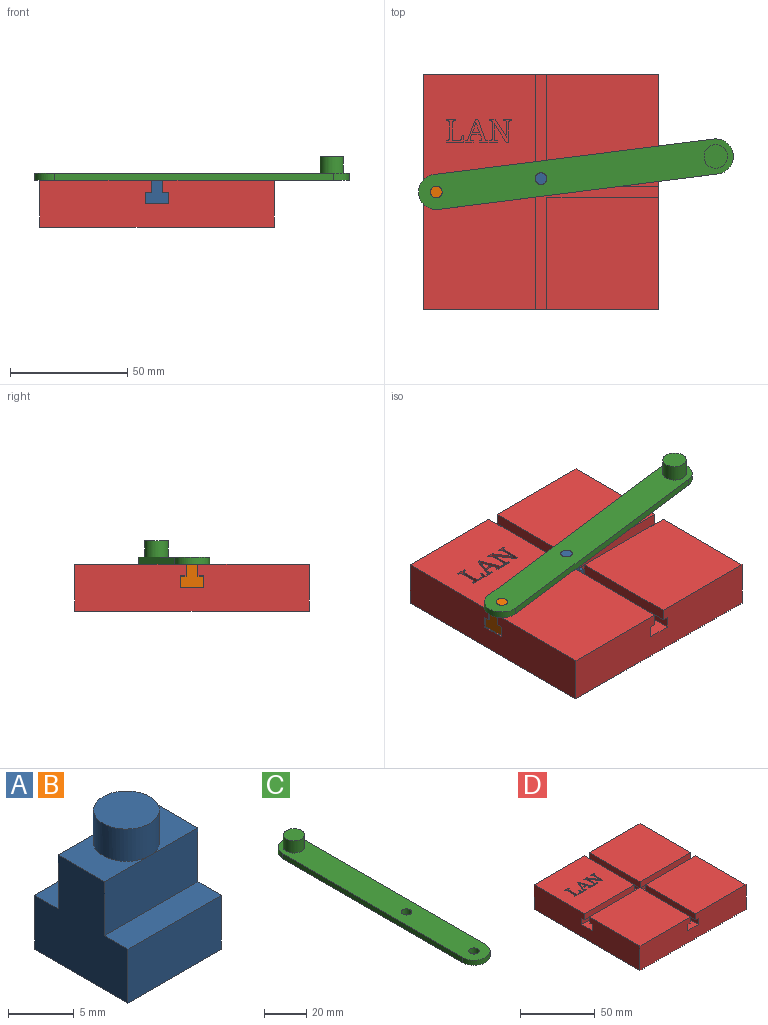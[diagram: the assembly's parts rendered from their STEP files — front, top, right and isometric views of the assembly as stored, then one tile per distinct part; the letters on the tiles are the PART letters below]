
ASSEMBLY  parts=4 mates=4
PART A: 13 faces, bbox 10x10x13 mm
  f0: plane 5x4.83mm, normal (0,0,1), area 14.3mm2, adj f2,f8,f10,f11
  f1: plane 5.17x5mm, normal (0,0,1), area 16mm2, adj f2,f8,f9,f11
  f2: plane 10x5mm, normal (0,1,0), area 50mm2, adj f0,f1,f3,f9,f10
  f3: plane 10x2.5mm, normal (0,0,1), area 25mm2, adj f2,f4,f9,f10
  f4: plane 10x5mm, normal (0,1,0), area 50mm2, adj f3,f5,f9,f10
  f5: plane 10x10mm, normal (0,0,-1), area 100mm2, adj f4,f6,f9,f10
  f6: plane 10x5mm, normal (0,-1,0), area 50mm2, adj f5,f7,f9,f10
  f7: plane 10x2.5mm, normal (0,0,1), area 25mm2, adj f6,f8,f9,f10
  f8: plane 10x5mm, normal (0,-1,0), area 50mm2, adj f0,f1,f7,f9,f10
  f9: plane 10x10mm, normal (1,0,0), area 75mm2, adj f1,f2,f3,f4,f5,f6,f7,f8
  f10: plane 10x10mm, normal (-1,0,0), area 75mm2, adj f0,f2,f3,f4,f5,f6,f7,f8
  f11: cylinder r=2.5mm len=5mm, axis (0,0,-1), area 47.1mm2, adj f0,f1,f12
  f12: plane 5x5mm, normal (0,0,1), area 19.6mm2, adj f11
PART B: same geometry as A
PART C: 10 faces, bbox 15x135x10 mm
  f0: plane 120x3mm, normal (1,0,0), area 360mm2, adj f1,f3,f6,f7
  f1: cylinder r=7.5mm len=15mm, axis (0,0,-1), area 70.7mm2, adj f0,f2,f6,f7
  f2: plane 120x3mm, normal (-1,0,0), area 360mm2, adj f1,f3,f6,f7
  f3: cylinder r=7.5mm len=15mm, axis (0,0,-1), area 70.7mm2, adj f0,f2,f6,f7
  f4: cylinder r=2.5mm len=5mm, axis (0,0,-1), area 47.1mm2, adj f6,f7
  f5: cylinder r=2.5mm len=5mm, axis (0,0,-1), area 47.1mm2, adj f6,f7
  f6: plane 135x15mm, normal (0,0,1), area 1858.9mm2, adj f0,f1,f2,f3,f4,f5,f8
  f7: plane 135x15mm, normal (0,0,-1), area 1937.4mm2, adj f0,f1,f2,f3,f4,f5
  f8: cylinder r=5mm len=10mm, axis (0,0,-1), area 219.9mm2, adj f6,f9
  f9: plane 10x10mm, normal (0,0,1), area 78.5mm2, adj f8
PART D: 144 faces, bbox 100x100x20 mm
  f0: plane 47.5x47.5mm, normal (0,0,1), area 2166.6mm2, adj f12,f13,f16,f25,f38,f39,f40,f41
  f1: plane 47.5x47.5mm, normal (0,0,1), area 2256.2mm2, adj f6,f10,f11,f27
  f2: plane 47.5x47.5mm, normal (0,0,1), area 2256.3mm2, adj f5,f10,f13,f23
  f3: plane 47.5x47.5mm, normal (0,0,-1), area 231.2mm2, adj f12,f13,f16,f21,f22,f25
  f4: plane 47.5x47.5mm, normal (0,0,-1), area 231.3mm2, adj f6,f7,f10,f11,f27,f29
  f5: plane 47.5x5mm, normal (1,0,0), area 237.5mm2, adj f2,f10,f15,f23
  f6: plane 47.5x5mm, normal (-1,0,0), area 237.5mm2, adj f1,f4,f10,f27
  f7: plane 45x5mm, normal (-1,0,0), area 225mm2, adj f4,f10,f20,f29
  f8: plane 45x5mm, normal (1,0,0), area 225mm2, adj f10,f15,f20,f24
  f9: plane 47.5x47.5mm, normal (0,0,1), area 2256.3mm2, adj f11,f12,f17,f26
  f10: plane 100x20mm, normal (0,-1,0), area 1925mm2, adj f1,f2,f4,f5,f6,f7,f8,f11
  f11: plane 100x20mm, normal (1,0,0), area 1925mm2, adj f1,f4,f9,f10,f12,f14,f18,f20
  f12: plane 100x20mm, normal (0,1,0), area 1925mm2, adj f0,f3,f9,f11,f13,f14,f16,f17
  f13: plane 100x20mm, normal (-1,0,0), area 1925mm2, adj f0,f2,f3,f10,f12,f14,f15,f20
  f14: plane 100x100mm, normal (0,0,-1), area 10000mm2, adj f10,f11,f12,f13
  f15: plane 47.5x47.5mm, normal (0,0,-1), area 231.2mm2, adj f5,f8,f10,f13,f23,f24
  f16: plane 47.5x5mm, normal (1,0,0), area 237.5mm2, adj f0,f3,f12,f25
  f17: plane 47.5x5mm, normal (-1,0,0), area 237.5mm2, adj f9,f12,f18,f26
  f18: plane 47.5x47.5mm, normal (0,0,-1), area 231.2mm2, adj f11,f12,f17,f19,f26,f28
  f19: plane 45x5mm, normal (-1,0,0), area 225mm2, adj f12,f18,f20,f28
  f20: plane 100x100mm, normal (0,0,1), area 1900mm2, adj f7,f8,f10,f11,f12,f13,f19,f21
  f21: plane 45x5mm, normal (1,0,0), area 225mm2, adj f3,f12,f20,f22
  f22: plane 45x5mm, normal (0,-1,0), area 225mm2, adj f3,f13,f20,f21
  f23: plane 47.5x5mm, normal (0,1,0), area 237.5mm2, adj f2,f5,f13,f15
  f24: plane 45x5mm, normal (0,1,0), area 225mm2, adj f8,f13,f15,f20
  f25: plane 47.5x5mm, normal (0,-1,0), area 237.5mm2, adj f0,f3,f13,f16
  f26: plane 47.5x5mm, normal (0,-1,0), area 237.5mm2, adj f9,f11,f17,f18
  f27: plane 47.5x5mm, normal (0,1,0), area 237.5mm2, adj f1,f4,f6,f11
  f28: plane 45x5mm, normal (0,-1,0), area 225mm2, adj f11,f18,f19,f20
  f29: plane 45x5mm, normal (0,1,0), area 225mm2, adj f4,f7,f11,f20
  f30: extruded ~3x1.15mm, area 3.6mm2, adj f31,f69,f70,f143
  f31: plane 3x2.41mm, normal (0.94,0.33,0), area 7.7mm2, adj f30,f32,f70,f143
  f32: plane 3.1x3mm, normal (0,-1,0), area 9.3mm2, adj f31,f33,f70,f143
  f33: plane 3x2.53mm, normal (-0.94,0.35,0), area 8.1mm2, adj f32,f34,f70,f143
  f34: extruded ~3x0.59mm, area 1.9mm2, adj f33,f35,f70,f143
  f35: extruded ~3x0.51mm, area 1.6mm2, adj f34,f36,f70,f143
  f36: extruded ~3x0.47mm, area 1.5mm2, adj f35,f37,f70,f143
  f37: extruded ~3x0.48mm, area 1.5mm2, adj f36,f69,f70,f143
  f38: plane 3x1.45mm, normal (-0.94,0.34,0), area 4.6mm2, adj f0,f39,f68,f70
  f39: plane 3.62x3mm, normal (0,1,0), area 10.9mm2, adj f0,f38,f40,f70
  f40: plane 3x1.54mm, normal (0.94,0.34,0), area 4.9mm2, adj f0,f39,f41,f70
  f41: extruded ~3x0.28mm, area 0.9mm2, adj f0,f40,f42,f70
  f42: extruded ~3x0.24mm, area 0.7mm2, adj f0,f41,f43,f70
  f43: extruded ~3x0.83mm, area 3.6mm2, adj f0,f42,f44,f70
  f44: plane 3x0.32mm, normal (0,-1,0), area 0.9mm2, adj f0,f43,f45,f70
  f45: plane 3x0.58mm, normal (1,0,0), area 1.7mm2, adj f0,f44,f46,f70
  f46: plane 3.79x3mm, normal (0,1,0), area 11.4mm2, adj f0,f45,f47,f70
  f47: plane 3x0.58mm, normal (-1,0,0), area 1.7mm2, adj f0,f46,f48,f70
  f48: plane 3x0.18mm, normal (0,-1,0), area 0.5mm2, adj f0,f47,f49,f70
  f49: extruded ~3x0.35mm, area 1.1mm2, adj f0,f48,f50,f70
  f50: extruded ~3x0.26mm, area 0.9mm2, adj f0,f49,f51,f70
  f51: extruded ~3x0.23mm, area 0.9mm2, adj f0,f50,f52,f70
  f52: extruded ~3x0.36mm, area 1.2mm2, adj f0,f51,f53,f70
  f53: plane 8.52x3.11mm, normal (-0.94,-0.34,0), area 27.2mm2, adj f0,f52,f54,f70
  f54: plane 3x1.08mm, normal (0,-1,0), area 3.2mm2, adj f0,f53,f55,f70
  f55: plane 8.18x3.05mm, normal (0.94,-0.35,0), area 26.2mm2, adj f0,f54,f56,f70
  f56: extruded ~3x0.54mm, area 1.8mm2, adj f0,f55,f57,f70
  f57: extruded ~3x0.33mm, area 1.2mm2, adj f0,f56,f58,f70
  f58: extruded ~3x0.26mm, area 0.9mm2, adj f0,f57,f59,f70
  f59: extruded ~3x0.34mm, area 1mm2, adj f0,f58,f60,f70
  f60: plane 3x0.26mm, normal (0,-1,0), area 0.8mm2, adj f0,f59,f61,f70
  f61: plane 3x0.58mm, normal (1,0,0), area 1.7mm2, adj f0,f60,f62,f70
  f62: plane 3.36x3mm, normal (0,1,0), area 10.1mm2, adj f0,f61,f63,f70
  f63: plane 3x0.58mm, normal (-1,0,0), area 1.7mm2, adj f0,f62,f64,f70
  f64: plane 3x0.32mm, normal (0,-1,0), area 0.9mm2, adj f0,f63,f65,f70
  f65: extruded ~3x0.69mm, area 2.2mm2, adj f0,f64,f66,f70
  f66: extruded ~3x0.51mm, area 1.7mm2, adj f0,f65,f67,f70
  f67: extruded ~3x0.27mm, area 0.8mm2, adj f0,f66,f68,f70
  f68: extruded ~3x0.32mm, area 1mm2, adj f0,f38,f67,f70
  f69: extruded ~3x1.03mm, area 3.2mm2, adj f30,f37,f70,f143
  f70: plane 9.83x9.71mm, normal (0,0,1), area 27.1mm2, adj f30,f31,f32,f33,f34,f35,f36,f37
  f71: plane 7.94x5.16mm, normal (0.84,0.55,0), area 28.4mm2, adj f0,f72,f110,f111
  f72: plane 3x0.98mm, normal (0,1,0), area 2.9mm2, adj f0,f71,f73,f111
  f73: plane 8.26x3mm, normal (-1,0,0), area 24.8mm2, adj f0,f72,f74,f111
  f74: extruded ~3x0.52mm, area 1.6mm2, adj f0,f73,f75,f111
  f75: extruded ~3x0.3mm, area 1.2mm2, adj f0,f74,f76,f111
  f76: extruded ~3x0.36mm, area 1.2mm2, adj f0,f75,f77,f111
  f77: extruded ~3x0.44mm, area 1.3mm2, adj f0,f76,f78,f111
  f78: plane 3x0.17mm, normal (0,1,0), area 0.5mm2, adj f0,f77,f79,f111
  f79: plane 3x0.58mm, normal (-1,0,0), area 1.7mm2, adj f0,f78,f80,f111
  f80: plane 3.46x3mm, normal (0,-1,0), area 10.4mm2, adj f0,f79,f81,f111
  f81: plane 3x0.58mm, normal (1,0,0), area 1.7mm2, adj f0,f80,f82,f111
  f82: plane 3x0.18mm, normal (0,1,0), area 0.5mm2, adj f0,f81,f83,f111
  f83: extruded ~3x0.43mm, area 1.3mm2, adj f0,f82,f84,f111
  f84: extruded ~3x0.36mm, area 1.2mm2, adj f0,f83,f85,f111
  f85: extruded ~3x0.29mm, area 1.1mm2, adj f0,f84,f86,f111
  f86: extruded ~3x0.49mm, area 1.5mm2, adj f0,f85,f87,f111
  f87: plane 6.1x3mm, normal (1,0,0), area 18.3mm2, adj f0,f86,f88,f111
  f88: plane 7.61x4.93mm, normal (-0.84,-0.54,0), area 27.2mm2, adj f0,f87,f89,f111
  f89: plane 3x2.52mm, normal (0,-1,0), area 7.6mm2, adj f0,f88,f90,f111
  f90: plane 3x0.58mm, normal (1,0,0), area 1.7mm2, adj f0,f89,f91,f111
  f91: plane 3x0.17mm, normal (0,1,0), area 0.5mm2, adj f0,f90,f92,f111
  f92: extruded ~3x0.43mm, area 1.3mm2, adj f0,f91,f93,f111
  f93: extruded ~3x0.36mm, area 1.2mm2, adj f0,f92,f94,f111
  f94: extruded ~3x0.29mm, area 1.1mm2, adj f0,f93,f95,f111
  f95: extruded ~3x0.49mm, area 1.5mm2, adj f0,f94,f96,f111
  f96: plane 6.75x3mm, normal (1,0,0), area 20.3mm2, adj f0,f95,f97,f111
  f97: extruded ~3x0.52mm, area 1.6mm2, adj f0,f96,f98,f111
  f98: extruded ~3x0.3mm, area 1.2mm2, adj f0,f97,f99,f111
  f99: extruded ~3x0.36mm, area 1.2mm2, adj f0,f98,f100,f111
  f100: extruded ~3x0.44mm, area 1.3mm2, adj f0,f99,f101,f111
  f101: plane 3x0.17mm, normal (0,-1,0), area 0.5mm2, adj f0,f100,f102,f111
  f102: plane 3x0.58mm, normal (1,0,0), area 1.7mm2, adj f0,f101,f103,f111
  f103: plane 3.46x3mm, normal (0,1,0), area 10.4mm2, adj f0,f102,f104,f111
  f104: plane 3x0.58mm, normal (-1,0,0), area 1.7mm2, adj f0,f103,f105,f111
  f105: plane 3x0.18mm, normal (0,-1,0), area 0.5mm2, adj f0,f104,f106,f111
  f106: extruded ~3x0.44mm, area 1.3mm2, adj f0,f105,f107,f111
  f107: extruded ~3x0.36mm, area 1.2mm2, adj f0,f106,f108,f111
  f108: extruded ~3x0.3mm, area 1.2mm2, adj f0,f107,f109,f111
  f109: extruded ~3x0.52mm, area 1.6mm2, adj f0,f108,f110,f111
  f110: plane 6.37x3mm, normal (-1,0,0), area 19.1mm2, adj f0,f71,f109,f111
  f111: plane 9.83x9.59mm, normal (0,0,1), area 34mm2, adj f71,f72,f73,f74,f75,f76,f77,f78
  f112: plane 3x0.58mm, normal (1,0,0), area 1.7mm2, adj f0,f113,f141,f142
  f113: plane 7.38x3mm, normal (0,1,0), area 22.1mm2, adj f0,f112,f114,f142
  f114: plane 3x2.96mm, normal (-1,0.03,0), area 8.9mm2, adj f0,f113,f115,f142
  f115: plane 3x0.72mm, normal (0,-1,0), area 2.2mm2, adj f0,f114,f116,f142
  f116: plane 3x1.03mm, normal (0.99,-0.13,0), area 3.1mm2, adj f0,f115,f117,f142
  f117: extruded ~3x0.44mm, area 1.4mm2, adj f0,f116,f118,f142
  f118: extruded ~3x0.4mm, area 1.4mm2, adj f0,f117,f119,f142
  f119: extruded ~3x0.36mm, area 1.4mm2, adj f0,f118,f120,f142
  f120: extruded ~3x0.53mm, area 1.6mm2, adj f0,f119,f121,f142
  f121: plane 3x2.72mm, normal (0,-1,0), area 8.1mm2, adj f0,f120,f122,f142
  f122: plane 7.63x3mm, normal (-1,0,0), area 22.9mm2, adj f0,f121,f123,f142
  f123: extruded ~3x0.49mm, area 1.5mm2, adj f0,f122,f124,f142
  f124: extruded ~3x0.29mm, area 1.1mm2, adj f0,f123,f125,f142
  f125: extruded ~3x0.36mm, area 1.2mm2, adj f0,f124,f126,f142
  f126: extruded ~3x0.43mm, area 1.3mm2, adj f0,f125,f127,f142
  f127: plane 3x0.18mm, normal (0,1,0), area 0.5mm2, adj f0,f126,f128,f142
  f128: plane 3x0.58mm, normal (-1,0,0), area 1.7mm2, adj f0,f127,f129,f142
  f129: plane 4.01x3mm, normal (0,-1,0), area 12mm2, adj f0,f128,f130,f142
  f130: plane 3x0.58mm, normal (1,0,0), area 1.7mm2, adj f0,f129,f131,f142
  f131: plane 3x0.17mm, normal (0,1,0), area 0.5mm2, adj f0,f130,f132,f142
  f132: extruded ~3x0.44mm, area 1.3mm2, adj f0,f131,f133,f142
  f133: extruded ~3x0.36mm, area 1.2mm2, adj f0,f132,f134,f142
  f134: extruded ~3x0.3mm, area 1.2mm2, adj f0,f133,f135,f142
  f135: extruded ~3x0.52mm, area 1.6mm2, adj f0,f134,f136,f142
  f136: plane 6.7x3mm, normal (1,0,0), area 20.1mm2, adj f0,f135,f137,f142
  f137: extruded ~3x0.52mm, area 1.6mm2, adj f0,f136,f138,f142
  f138: extruded ~3x0.3mm, area 1.2mm2, adj f0,f137,f139,f142
  f139: extruded ~3x0.36mm, area 1.2mm2, adj f0,f138,f140,f142
  f140: extruded ~3x0.44mm, area 1.3mm2, adj f0,f139,f141,f142
  f141: plane 3x0.17mm, normal (0,-1,0), area 0.5mm2, adj f0,f112,f140,f142
  f142: plane 9.83x7.48mm, normal (0,0,1), area 21.8mm2, adj f112,f113,f114,f115,f116,f117,f118,f119
  f143: plane 4.59x3.1mm, normal (0,0,1), area 6.8mm2, adj f30,f31,f32,f33,f34,f35,f36,f37
PLACE A rot(axis=(0,0,-1),90deg) t=(-2.5,-37.01,-20)mm
PLACE B rot(axis=(-0.06,0.74,0.67),0deg) t=(-1.97,2.5,-20)mm
PLACE C rot(axis=(0,0,-1),82.8deg) t=(2.4,83.97,0)mm
PLACE D rot(axis=(1,0,0),0deg) t=(-2.5,2.5,-20)mm
MATE revolute C.f3 <-> B.f11  axis (0,0,1) through (-47.14,2.5,3)mm
MATE revolute A.f11 <-> C.f4  axis (0,0,1) through (-2.5,8.16,3)mm
MATE slider A.f9 <-> D.f10  axis (0,-1,0) through (-7.5,2.99,-5)mm
MATE slider B.f10 <-> D.f13  axis (-1,0,0) through (-51.97,7.5,-10)mm
